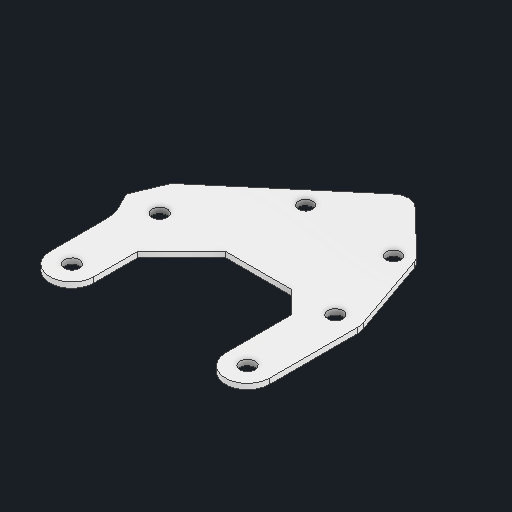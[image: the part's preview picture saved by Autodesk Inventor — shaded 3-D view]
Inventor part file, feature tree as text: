
AUTODESK INVENTOR PART (.ipt)
format: ipt  version: 2025 (Build 290162000, 162)  size: 156,672 bytes
history: native  units: in
note: dims shown in document units (in); Inventor stores cm internally (conversion verified against a paired STEP export)
features: other x6, sketch x1
ambient origin geometry x8: Origin, YZ Plane, XZ Plane, XY Plane, X Axis, Y Axis, Z Axis, Center Point
bodies: Solid1 (feature_tree)
feature tree (7):
  other  "gusset.ipt"
  other  "Blocks"
  other  "main"
  other  "Solid1::gusset.ipt"
  other  "TaggingFeature1"
  sketch  "Sketch1"  dims[d0=0.3937in d1=0.375in d2=0.5in d3=0.5in d4=0.25in d5=0.25in d6=0.164in d7=0.1875in d9=0.125in d12=1.911in d14=0.125in d15=0.5in d16=1.0in d18=0.25in d17=1.9106in]
  other  "main:1"
